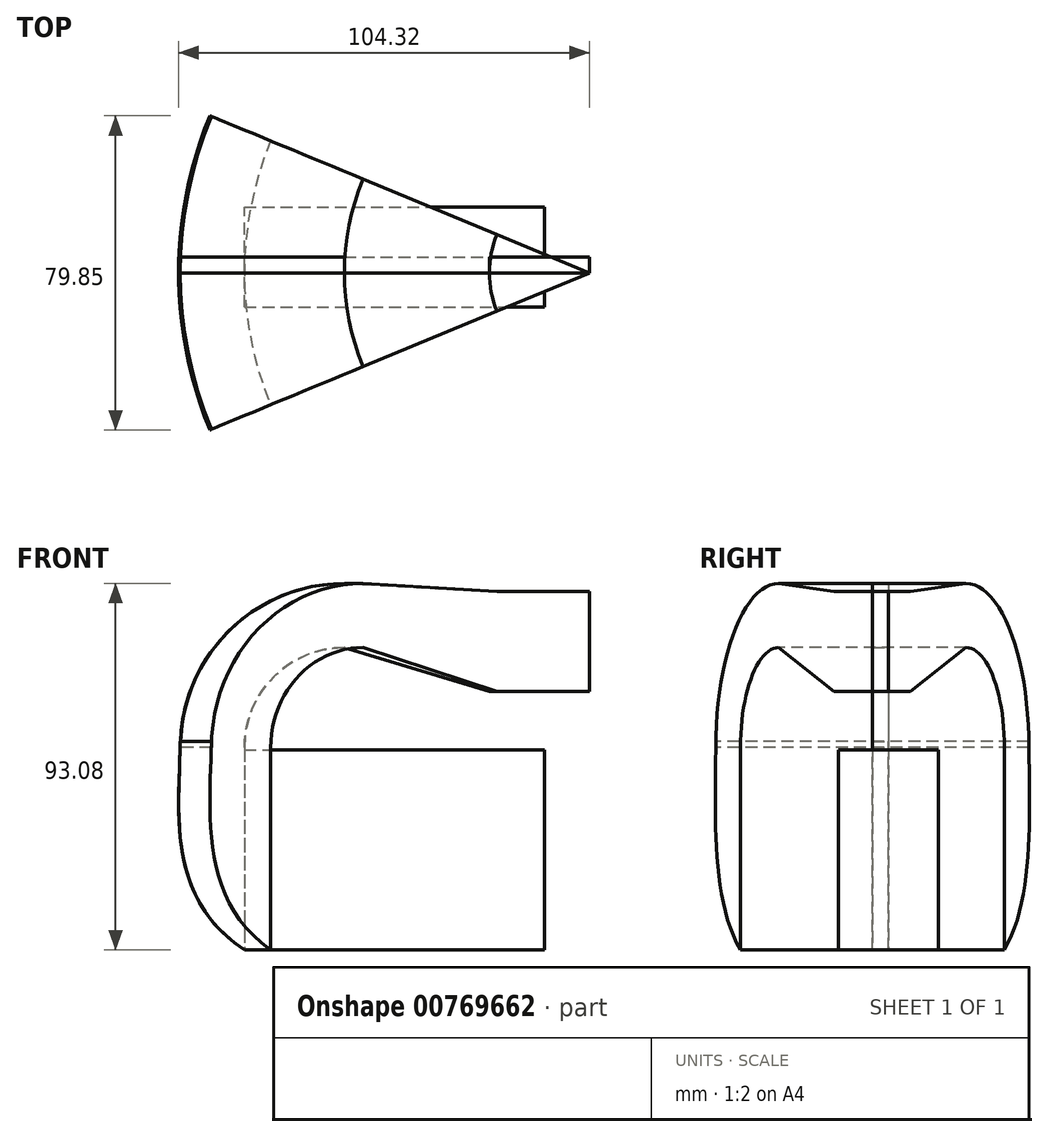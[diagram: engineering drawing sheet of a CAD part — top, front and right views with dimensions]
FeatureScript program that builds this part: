
annotation { "Feature Type Name" : "Feature", "Feature Type Description" : "" }
export const myFeature = defineFeature(function(context is Context, id is Id, definition is map)
    precondition{}
    {
        {
            var Q0;
            Q0=qCreatedBy(makeId("Front.planeOp"),FACE);
            var sketch = newSketch(context, id + "F0", { "sketchPlane" : qUnion([Q0])});
            skLineSegment(sketch, "E0.bottom", {"start": v(-38.1, 25.4) * mm, "end": v(38.1, 25.4) * mm});
            skLineSegment(sketch, "E0.top", {"start": v(-38.1, -25.4) * mm, "end": v(38.1, -25.4) * mm});
            skLineSegment(sketch, "E0.left", {"start": v(-38.1, 25.4) * mm, "end": v(-38.1, -25.4) * mm});
            skLineSegment(sketch, "E0.right", {"start": v(38.1, 25.4) * mm, "end": v(38.1, -25.4) * mm});
            skPoint(sketch, "E0.middle", {"position": v(0, 0) * mm});
            skLineSegment(sketch, "E1.bottom", {"start": v(49.52, 65.66) * mm, "end": v(24.12, 65.66) * mm});
            skLineSegment(sketch, "E1.top", {"start": v(49.52, 40.26) * mm, "end": v(24.12, 40.26) * mm});
            skLineSegment(sketch, "E1.left", {"start": v(49.52, 65.66) * mm, "end": v(49.52, 40.26) * mm});
            skLineSegment(sketch, "E1.right", {"start": v(24.12, 65.66) * mm, "end": v(24.12, 40.26) * mm});
            skPoint(sketch, "E1.middle", {"position": v(36.82, 52.96) * mm});
            skLineSegment(sketch, "E2", {"start": v(-38.1, 25.4) * mm, "end": v(-38.1, 26) * mm});
            skArc(sketch, "E3", {"start": v(-38.1, 26) * mm, "mid": v(-30.66, 43.96) * mm, "end": v(-12.7, 51.4) * mm});
            skArc(sketch, "E4.1", {"start": v(-54.38, 26) * mm, "mid": v(-42.17, 55.48) * mm, "end": v(-12.7, 67.68) * mm});
            skLineSegment(sketch, "E4.2", {"start": v(-54.38, 26) * mm, "end": v(-54.38, 31.52) * mm});
            skFitSpline(sketch, "E5", {"points": [v(-38.1, -25.4) * mm, v(-54.38, 31.52) * mm], "startDerivative": vector(-64.93, 42.24) * mm, "endDerivative": vector(-1.15, 53.04) * mm});
            skLineSegment(sketch, "E6", {"start": v(-12.7, 67.68) * mm, "end": v(24.12, 65.66) * mm});
            skLineSegment(sketch, "E7", {"start": v(-12.7, 51.4) * mm, "end": v(24.12, 40.26) * mm});
            skSolve(sketch);
        }
        {
            var Q0;
            Q0=makeQuery(id+"F0.imprint","IMPRINT",FACE,{"disambiguationData":[TD([[makeQuery(id+"F0.imprint","IMPRINT",EDGE,{"derivedFrom":sQuery(id+"F0.wireOp",EDGE,"E0.bottom")}),-1.0]])]});
            extrude(context, id + "F1", {"entities" : qUnion([Q0]), "surfaceOperationType" : NewSurfaceOperationType.ADD, "endBound" : BoundingType.SYMMETRIC, "depth" : 25.4 * mm, "offsetDistance" : 25.4 * mm});
        }
        {
            var Q0;
            {var subQ0=sQuery(id+"F0.wireOp",EDGE,"E0.left");Q0=makeQuery(id+"F0.imprint","IMPRINT",FACE,{"disambiguationData":[TD([[makeQuery(id+"F0.imprint","IMPRINT",EDGE,{"derivedFrom":subQ0}),-1.0]])]});}
            var Q1;
            Q1=makeQuery(id+"F0.imprint","IMPRINT",FACE,{"disambiguationData":[TD([[makeQuery(id+"F0.imprint","IMPRINT",EDGE,{"derivedFrom":sQuery(id+"F0.wireOp",EDGE,"E1.bottom")}),1.0]])]});
            extrude(context, id + "F2", {"entities" : qUnion([Q0, Q1]), "depth" : 4.06 * mm, "offsetDistance" : 25.4 * mm});
        }
        {
            var Q0;
            Q0=makeQuery(id+"F2.opExtrude","CAP_FACE",FACE,{"disambiguationData":[OSD([sQuery(id+"F0.wireOp",EDGE,"E0.left"),sQuery(id+"F0.wireOp",EDGE,"E1.bottom"),sQuery(id+"F0.wireOp",EDGE,"E1.top"),sQuery(id+"F0.wireOp",EDGE,"E1.left"),sQuery(id+"F0.wireOp",EDGE,"E2"),sQuery(id+"F0.wireOp",EDGE,"E3"),sQuery(id+"F0.wireOp",EDGE,"E4.1"),sQuery(id+"F0.wireOp",EDGE,"E4.2"),sQuery(id+"F0.wireOp",EDGE,"E5"),sQuery(id+"F0.wireOp",EDGE,"E6"),sQuery(id+"F0.wireOp",EDGE,"E7")])],"isStart":false});
            var Q1;
            Q1=makeQuery(id+"F2.opExtrude","CAP_EDGE",EDGE,{"disambiguationData":[OSD([sQuery(id+"F0.wireOp",EDGE,"E1.left")])],"isStart":false});
            revolve(context, id + "F3", {"surfaceOperationType" : NewSurfaceOperationType.NEW, "entities" : qUnion([Q0]), "axis" : qUnion([Q1]), "revolveType" : RevolveType.SYMMETRIC, "angle" : 45 * degree});
        }
    });
